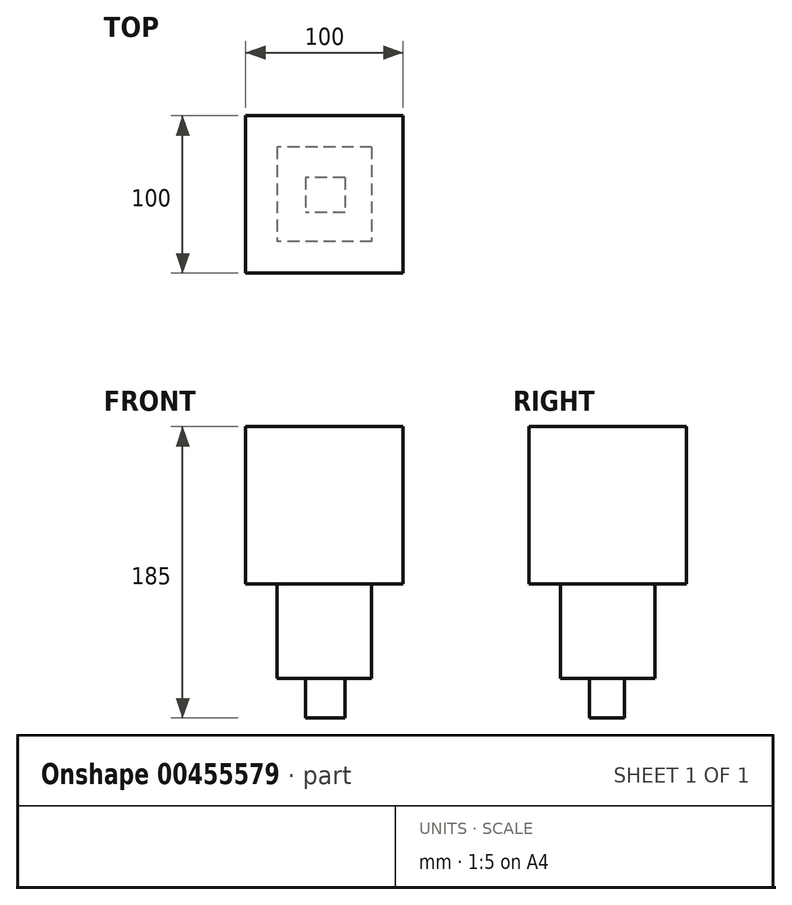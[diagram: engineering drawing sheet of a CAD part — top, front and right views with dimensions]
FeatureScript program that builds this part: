
annotation { "Feature Type Name" : "Feature", "Feature Type Description" : "" }
export const myFeature = defineFeature(function(context is Context, id is Id, definition is map)
    precondition{}
    {
        {
            var Q0;
            Q0=qCreatedBy(makeId("Top.planeOp"),FACE);
            var sketch = newSketch(context, id + "F0", { "sketchPlane" : qUnion([Q0])});
            skLineSegment(sketch, "E0.bottom", {"start": v(-50, 50) * mm, "end": v(50, 50) * mm});
            skLineSegment(sketch, "E0.top", {"start": v(-50, -50) * mm, "end": v(50, -50) * mm});
            skLineSegment(sketch, "E0.left", {"start": v(-50, 50) * mm, "end": v(-50, -50) * mm});
            skLineSegment(sketch, "E0.right", {"start": v(50, 50) * mm, "end": v(50, -50) * mm});
            skSolve(sketch);
        }
        {
            var Q0;
            Q0=makeQuery(id+"F0.imprint","IMPRINT",FACE,{"disambiguationData":[TD([[makeQuery(id+"F0.imprint","IMPRINT",EDGE,{"derivedFrom":sQuery(id+"F0.wireOp",EDGE,"E0.bottom")}),-1.0]])]});
            extrude(context, id + "F1", {"entities" : qUnion([Q0]), "depth" : 100 * mm});
        }
        {
            var Q0;
            Q0=qCreatedBy(makeId("Top.planeOp"),FACE);
            var sketch = newSketch(context, id + "F2", { "sketchPlane" : qUnion([Q0])});
            skLineSegment(sketch, "E1.bottom", {"start": v(36.72, -40.1) * mm, "end": v(-36.72, -40.1) * mm});
            skLineSegment(sketch, "E1.top", {"start": v(36.72, 40.1) * mm, "end": v(-36.72, 40.1) * mm});
            skLineSegment(sketch, "E1.left", {"start": v(36.72, -40.1) * mm, "end": v(36.72, 40.1) * mm});
            skLineSegment(sketch, "E1.right", {"start": v(-36.72, -40.1) * mm, "end": v(-36.72, 40.1) * mm});
            skLineSegment(sketch, "E2.bottom", {"start": v(20.78, -19.33) * mm, "end": v(-20.78, -19.33) * mm});
            skLineSegment(sketch, "E2.top", {"start": v(20.78, 19.33) * mm, "end": v(-20.78, 19.33) * mm});
            skLineSegment(sketch, "E2.left", {"start": v(20.78, -19.33) * mm, "end": v(20.78, 19.33) * mm});
            skLineSegment(sketch, "E2.right", {"start": v(-20.78, -19.33) * mm, "end": v(-20.78, 19.33) * mm});
            skLineSegment(sketch, "E3.bottom", {"start": v(-10.63, -6.76) * mm, "end": v(10.63, -6.76) * mm});
            skLineSegment(sketch, "E3.top", {"start": v(-10.63, 6.76) * mm, "end": v(10.63, 6.76) * mm});
            skLineSegment(sketch, "E3.left", {"start": v(-10.63, -6.76) * mm, "end": v(-10.63, 6.76) * mm});
            skLineSegment(sketch, "E3.right", {"start": v(10.63, -6.76) * mm, "end": v(10.63, 6.76) * mm});
            skSolve(sketch);
        }
        {
            var Q0;
            Q0=makeQuery(id+"F2.imprint","IMPRINT",FACE,{"disambiguationData":[TD([[makeQuery(id+"F2.imprint","IMPRINT",EDGE,{"derivedFrom":sQuery(id+"F2.wireOp",EDGE,"E3.bottom")}),1.0]])]});
            extrude(context, id + "F3", {"entities" : qUnion([Q0]), "operationType" : NewBodyOperationType.ADD, "oppositeDirection" : true, "depth" : 20 * mm});
        }
        {
            var Q0;
            Q0=qCreatedBy(makeId("Top.planeOp"),FACE);
            var sketch = newSketch(context, id + "F4", { "sketchPlane" : qUnion([Q0])});
            skLineSegment(sketch, "E4.bottom", {"start": v(30, 30) * mm, "end": v(-30, 30) * mm});
            skLineSegment(sketch, "E4.top", {"start": v(30, -30) * mm, "end": v(-30, -30) * mm});
            skLineSegment(sketch, "E4.left", {"start": v(30, 30) * mm, "end": v(30, -30) * mm});
            skLineSegment(sketch, "E4.right", {"start": v(-30, 30) * mm, "end": v(-30, -30) * mm});
            skSolve(sketch);
        }
        {
            var Q0;
            Q0=makeQuery(id+"F4.imprint","IMPRINT",FACE,{"disambiguationData":[TD([[makeQuery(id+"F4.imprint","IMPRINT",EDGE,{"derivedFrom":sQuery(id+"F4.wireOp",EDGE,"E4.bottom")}),1.0]])]});
            extrude(context, id + "F5", {"entities" : qUnion([Q0]), "operationType" : NewBodyOperationType.ADD, "oppositeDirection" : true, "depth" : 60 * mm});
        }
        {
            var Q0;
            Q0=makeQuery(id+"F5.opExtrude","CAP_FACE",FACE,{"disambiguationData":[OSD([sQuery(id+"F4.wireOp",EDGE,"E4.bottom"),sQuery(id+"F4.wireOp",EDGE,"E4.top"),sQuery(id+"F4.wireOp",EDGE,"E4.left"),sQuery(id+"F4.wireOp",EDGE,"E4.right")])],"isStart":false});
            var sketch = newSketch(context, id + "F6", { "sketchPlane" : qUnion([Q0])});
            skSolve(sketch);
        }
        {
            var Q0;
            Q0=makeQuery(id+"F6.imprint","IMPRINT",FACE,{"disambiguationData":[TD([[makeQuery(id+"F6.imprint","IMPRINT",EDGE,{"derivedFrom":makeQuery(id+"F5.opExtrude","CAP_EDGE",EDGE,{"disambiguationData":[OSD([sQuery(id+"F4.wireOp",EDGE,"E4.bottom")])],"isStart":false})}),-1.0]])]});
            var sketch = newSketch(context, id + "F7", { "sketchPlane" : qUnion([Q0])});
            skLineSegment(sketch, "E5.bottom", {"start": v(17.5, -13.53) * mm, "end": v(-17.5, -13.53) * mm});
            skLineSegment(sketch, "E5.top", {"start": v(17.5, 13.53) * mm, "end": v(-17.5, 13.53) * mm});
            skLineSegment(sketch, "E5.left", {"start": v(17.5, -13.53) * mm, "end": v(17.5, 13.53) * mm});
            skLineSegment(sketch, "E5.right", {"start": v(-17.5, -13.53) * mm, "end": v(-17.5, 13.53) * mm});
            skSolve(sketch);
        }
        {
            var Q0;
            Q0=makeQuery(id+"F6.imprint","IMPRINT",FACE,{"disambiguationData":[TD([[makeQuery(id+"F6.imprint","IMPRINT",EDGE,{"derivedFrom":makeQuery(id+"F5.opExtrude","CAP_EDGE",EDGE,{"disambiguationData":[OSD([sQuery(id+"F4.wireOp",EDGE,"E4.bottom")])],"isStart":false})}),-1.0]])]});
            var sketch = newSketch(context, id + "F8", { "sketchPlane" : qUnion([Q0])});
            skSolve(sketch);
        }
        {
            var Q0;
            Q0 = qSketchRegion(id + "F7", true);
            var Q1;
            Q1=makeQuery(id+"F6.imprint","IMPRINT",FACE,{"disambiguationData":[TD([[makeQuery(id+"F6.imprint","IMPRINT",EDGE,{"derivedFrom":makeQuery(id+"F5.opExtrude","CAP_EDGE",EDGE,{"disambiguationData":[OSD([sQuery(id+"F4.wireOp",EDGE,"E4.bottom")])],"isStart":false})}),-1.0]])]});
            extrude(context, id + "F9", {"entities" : qUnion([Q0, Q1]), "operationType" : NewBodyOperationType.ADD, "oppositeDirection" : true, "depth" : 100 * mm});
        }
        {
            var Q0;
            Q0=makeQuery(id+"F8.imprint","IMPRINT",FACE,{"disambiguationData":[TD([[makeQuery(id+"F8.imprint","IMPRINT",EDGE,{"derivedFrom":makeQuery(id+"F6.imprint","IMPRINT",EDGE,{"derivedFrom":makeQuery(id+"F5.opExtrude","CAP_EDGE",EDGE,{"disambiguationData":[OSD([sQuery(id+"F4.wireOp",EDGE,"E4.bottom")])],"isStart":false})})}),-1.0]])]});
            var sketch = newSketch(context, id + "F10", { "sketchPlane" : qUnion([Q0])});
            skLineSegment(sketch, "E6.bottom", {"start": v(13.05, -10.63) * mm, "end": v(-12.08, -10.63) * mm});
            skLineSegment(sketch, "E6.top", {"start": v(13.05, 11.6) * mm, "end": v(-12.08, 11.6) * mm});
            skLineSegment(sketch, "E6.left", {"start": v(13.05, -10.63) * mm, "end": v(13.05, 11.6) * mm});
            skLineSegment(sketch, "E6.right", {"start": v(-12.08, -10.63) * mm, "end": v(-12.08, 11.6) * mm});
            skSolve(sketch);
        }
        {
            var Q0;
            Q0 = qSketchRegion(id + "F10", true);
            var Q1;
            Q1=makeQuery(id+"F8.imprint","IMPRINT",FACE,{"disambiguationData":[TD([[makeQuery(id+"F8.imprint","IMPRINT",EDGE,{"derivedFrom":makeQuery(id+"F6.imprint","IMPRINT",EDGE,{"derivedFrom":makeQuery(id+"F5.opExtrude","CAP_EDGE",EDGE,{"disambiguationData":[OSD([sQuery(id+"F4.wireOp",EDGE,"E4.bottom")])],"isStart":false})})}),-1.0]])]});
            extrude(context, id + "F11", {"entities" : qUnion([Q0, Q1]), "operationType" : NewBodyOperationType.ADD, "oppositeDirection" : true, "depth" : 110 * mm});
        }
        {
            var Q0;
            Q0=makeQuery(id+"F10.imprint","IMPRINT",FACE,{"disambiguationData":[TD([[makeQuery(id+"F10.imprint","IMPRINT",EDGE,{"derivedFrom":sQuery(id+"F10.wireOp",EDGE,"E6.bottom")}),-1.0]])]});
            extrude(context, id + "F12", {"entities" : qUnion([Q0]), "operationType" : NewBodyOperationType.ADD, "depth" : 25 * mm});
        }
    });
